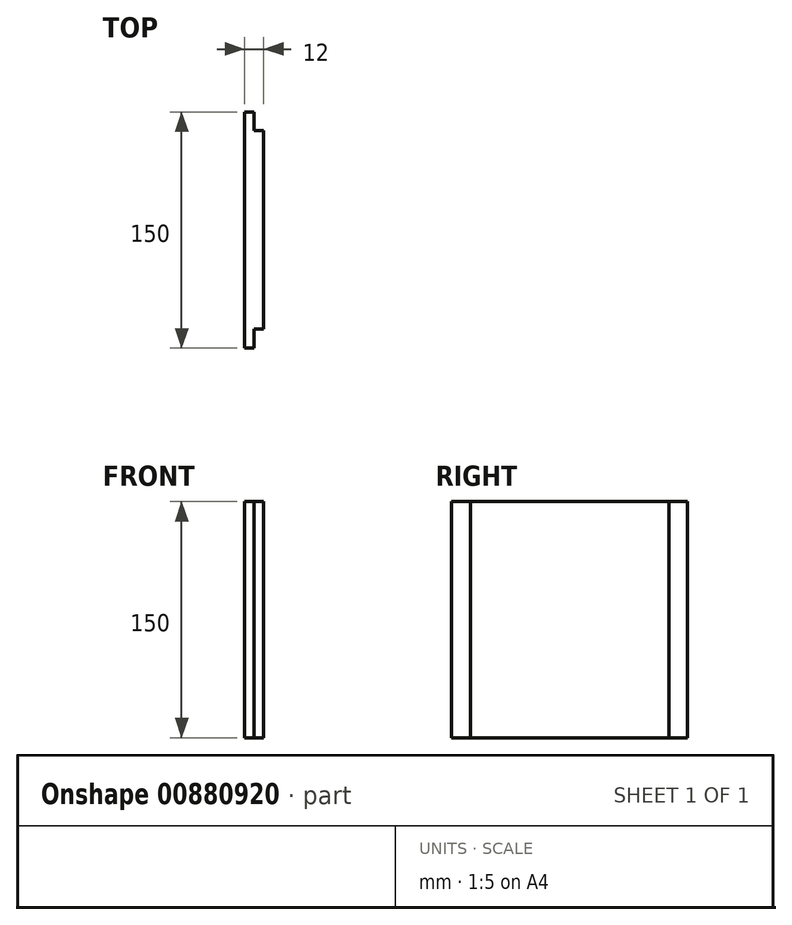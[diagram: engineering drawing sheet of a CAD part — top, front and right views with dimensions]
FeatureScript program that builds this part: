
annotation { "Feature Type Name" : "Feature", "Feature Type Description" : "" }
export const myFeature = defineFeature(function(context is Context, id is Id, definition is map)
    precondition{}
    {
        {
            var Q0;
            Q0=qCreatedBy(makeId("Top.planeOp"),FACE);
            var sketch = newSketch(context, id + "F0", { "sketchPlane" : qUnion([Q0])});
            skLineSegment(sketch, "E0.bottom", {"start": v(0, 75) * mm, "end": v(-6, 75) * mm});
            skLineSegment(sketch, "E0.top", {"start": v(0, -75) * mm, "end": v(-6, -75) * mm});
            skLineSegment(sketch, "E0.left", {"start": v(6, 63) * mm, "end": v(6, -63) * mm});
            skLineSegment(sketch, "E0.right", {"start": v(-6, 75) * mm, "end": v(-6, -75) * mm});
            skPoint(sketch, "E0.middle", {"position": v(0, 0) * mm});
            skLineSegment(sketch, "E1", {"start": v(0, 75) * mm, "end": v(0, 63) * mm});
            skLineSegment(sketch, "E2", {"start": v(0, 63) * mm, "end": v(6, 63) * mm});
            skPoint(sketch, "E3.orphan", {"position": v(6, 75) * mm});
            skLineSegment(sketch, "E4", {"start": v(0, -75) * mm, "end": v(0, -63) * mm});
            skLineSegment(sketch, "E5", {"start": v(0, -63) * mm, "end": v(6, -63) * mm});
            skPoint(sketch, "E6.orphan", {"position": v(6, -75) * mm});
            skSolve(sketch);
        }
        {
            var Q0;
            Q0=makeQuery(id+"F0.imprint","IMPRINT",FACE,{"disambiguationData":[TD([[makeQuery(id+"F0.imprint","IMPRINT",EDGE,{"derivedFrom":sQuery(id+"F0.wireOp",EDGE,"E0.bottom")}),1.0]])]});
            extrude(context, id + "F1", {"entities" : qUnion([Q0]), "endBound" : BoundingType.SYMMETRIC, "depth" : 150 * mm, "offsetDistance" : 25 * mm});
        }
    });
